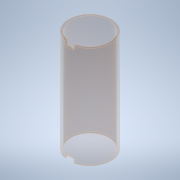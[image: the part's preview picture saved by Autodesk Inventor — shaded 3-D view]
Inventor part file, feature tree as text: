
AUTODESK INVENTOR PART (.ipt)
format: ipt  version: 2022 (Build 260153000, 153)  size: 144,896 bytes
history: native  units: in
note: dims shown in document units (in); Inventor stores cm internally (conversion verified against a paired STEP export)
features: sketch x2, extrude x1, revolve x1, fillet x1
ambient origin geometry x8: Origin, YZ Plane, XZ Plane, XY Plane, X Axis, Y Axis, Z Axis, Center Point
bodies: Body1 (feature_tree)
feature tree (5):
  extrude  "Extrusion3"  Depth=2.0315in
  revolve  "Revolution2"  [1 undecoded]
  fillet  "Fillet3"  Radius=0.1575in
  sketch  "Sketch5"  dims[d26=2.2677in d27=2.0315in]
  sketch  "Sketch6"  dims[d28=5.4488in d29=0.0in d31=0.2205in d32=0.1575in d33=0.2205in d34=0.1575in d35=0.086in d36=0.086in d37=0.0787in]
note: 1 required parameter value undecoded (feature->parameter linkage not recoverable at this tier; creation-order binding heuristic only, values carry confidence <= 0.55)
